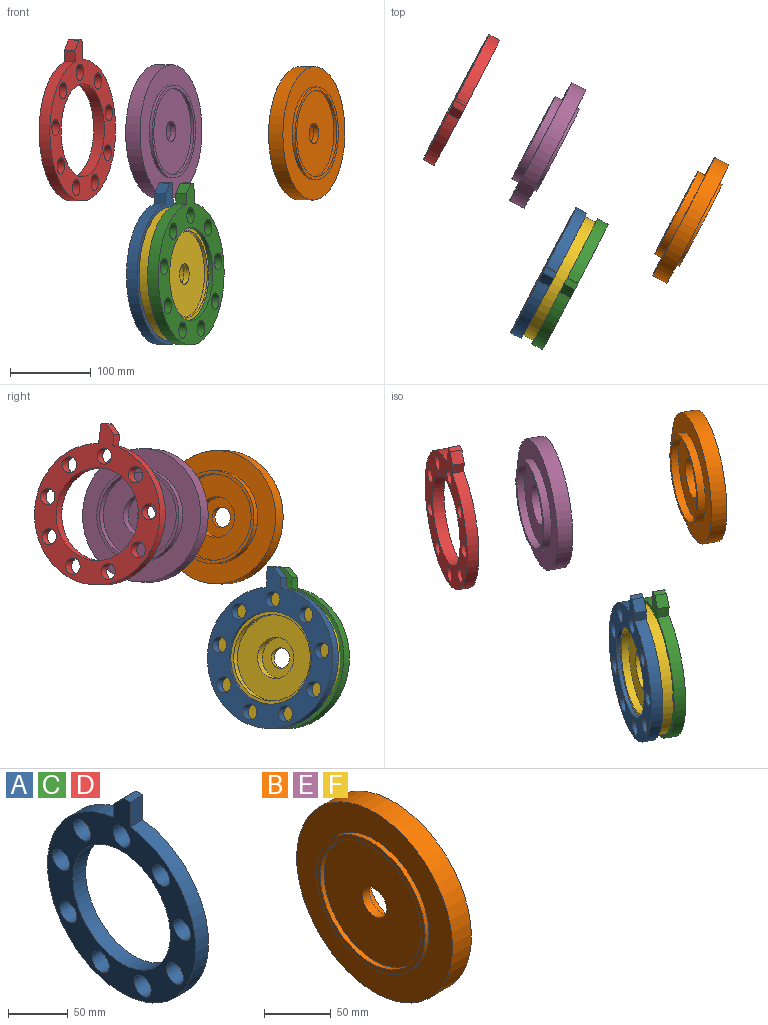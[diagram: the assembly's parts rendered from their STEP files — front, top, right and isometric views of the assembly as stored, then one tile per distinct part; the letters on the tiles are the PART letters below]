
ASSEMBLY  parts=6 mates=5
PART A: 17 faces, bbox 15x175x199.8 mm
  f0: plane 15x8mm, normal (0,0,1), area 120mm2, adj f1,f5,f6,f7
  f1: plane 25.4x15mm, normal (0,-1,0), area 381mm2, adj f0,f2,f5,f6
  f2: cylinder r=87.5mm len=175mm, axis (-1,0,0), area 7946mm2, adj f1,f4,f5,f6
  f3: cylinder r=57.5mm len=115mm, axis (-1,0,0), area 5419.2mm2, adj f5,f6
  f4: plane 15x13.4mm, normal (0,1,0), area 201mm2, adj f2,f5,f6,f7
  f5: plane 199.83x175mm, normal (1,0,0), area 11266.8mm2, adj f0,f1,f2,f3,f4,f7,f8,f9
  f6: plane 199.83x175mm, normal (-1,0,0), area 11266.8mm2, adj f0,f1,f2,f3,f4,f7,f8,f9
  f7: plane 15x12mm, normal (0,0.71,0.71), area 254.6mm2, adj f0,f4,f5,f6
  f8: cylinder r=10mm len=20mm, axis (1,0,0), area 942.5mm2, adj f5,f6
  f9: cylinder r=10mm len=20mm, axis (1,0,0), area 942.5mm2, adj f5,f6
  f10: cylinder r=10mm len=20mm, axis (1,0,0), area 942.5mm2, adj f5,f6
  f11: cylinder r=10mm len=20mm, axis (1,0,0), area 942.5mm2, adj f5,f6
  f12: cylinder r=10mm len=20mm, axis (1,0,0), area 942.5mm2, adj f5,f6
  f13: cylinder r=10mm len=20mm, axis (1,0,0), area 942.5mm2, adj f5,f6
  f14: cylinder r=10mm len=20mm, axis (1,0,0), area 942.5mm2, adj f5,f6
  f15: cylinder r=10mm len=20mm, axis (1,0,0), area 942.5mm2, adj f5,f6
  f16: cylinder r=10mm len=20mm, axis (1,0,0), area 942.5mm2, adj f5,f6
PART B: 14 faces, bbox 34x165x165 mm
  f0: plane 107x107mm, normal (1,0,0), area 6965.2mm2, adj f2,f11
  f1: plane 107x107mm, normal (-1,0,0), area 8485.3mm2, adj f4,f5
  f2: cylinder r=25.4mm len=50.8mm, axis (1,0,0), area 2026.8mm2, adj f0,f3
  f3: plane 50.8x50.8mm, normal (1,0,0), area 1520.1mm2, adj f2,f4
  f4: cylinder r=12.7mm len=25.4mm, axis (1,0,0), area 582.5mm2, adj f1,f3
  f5: cylinder r=53.5mm len=107mm, axis (1,0,0), area 1344.6mm2, adj f1,f6
  f6: plane 115x115mm, normal (-1,0,0), area 1394.9mm2, adj f5,f7
  f7: cylinder r=57.5mm len=115mm, axis (1,0,0), area 1445.1mm2, adj f6,f10
  f8: plane 165x165mm, normal (1,0,0), area 10995.6mm2, adj f9,f12
  f9: cylinder r=82.5mm len=165mm, axis (-1,0,0), area 10367.3mm2, adj f8,f10
  f10: plane 165x165mm, normal (-1,0,0), area 10995.6mm2, adj f7,f9
  f11: cylinder r=53.5mm len=107mm, axis (1,0,0), area 3361.5mm2, adj f0,f13
  f12: cylinder r=57.5mm len=115mm, axis (1,0,0), area 3612.8mm2, adj f8,f13
  f13: plane 115x115mm, normal (1,0,0), area 1394.9mm2, adj f11,f12
PART C: same geometry as A
PART D: same geometry as A
PART E: same geometry as B
PART F: same geometry as B
PLACE A rot(axis=(0,-0.02,1),152.3deg) t=(48.69,-72.3,14.62)mm
PLACE B rot(axis=(0,-0.01,1),152.3deg) t=(226.5,-8.39,188.43)mm
PLACE C rot(axis=(0,-0.02,1),152.3deg) t=(74.81,-86,14.28)mm
PLACE D rot(axis=(-0.01,-0.07,1),152.3deg) t=(-59.35,141.53,192.14)mm
PLACE E rot(axis=(0,-0.02,1),152.3deg) t=(49.8,84.28,190.72)mm
PLACE F rot(axis=(0,-0.02,1),152.3deg) t=(66.4,-81.59,14.39)mm
MATE cylindrical E.f7 <-> D.f3  axis (-0.89,0.46,0.01) through (27.66,95.89,191.01)mm
MATE cylindrical B.f7 <-> D.f3  axis (-0.89,0.46,0.01) through (204.36,3.22,188.71)mm
MATE cylindrical F.f7 <-> A.f3  axis (-0.89,0.46,0.01) through (44.26,-69.98,14.68)mm
MATE planar F.f9 <-> A.f6  axis (-0.89,0.46,0.01) through (48.69,-72.3,14.62)mm
MATE cylindrical C.f3 <-> F.f7  axis (0.89,-0.46,-0.01) through (68.17,-82.52,14.37)mm
